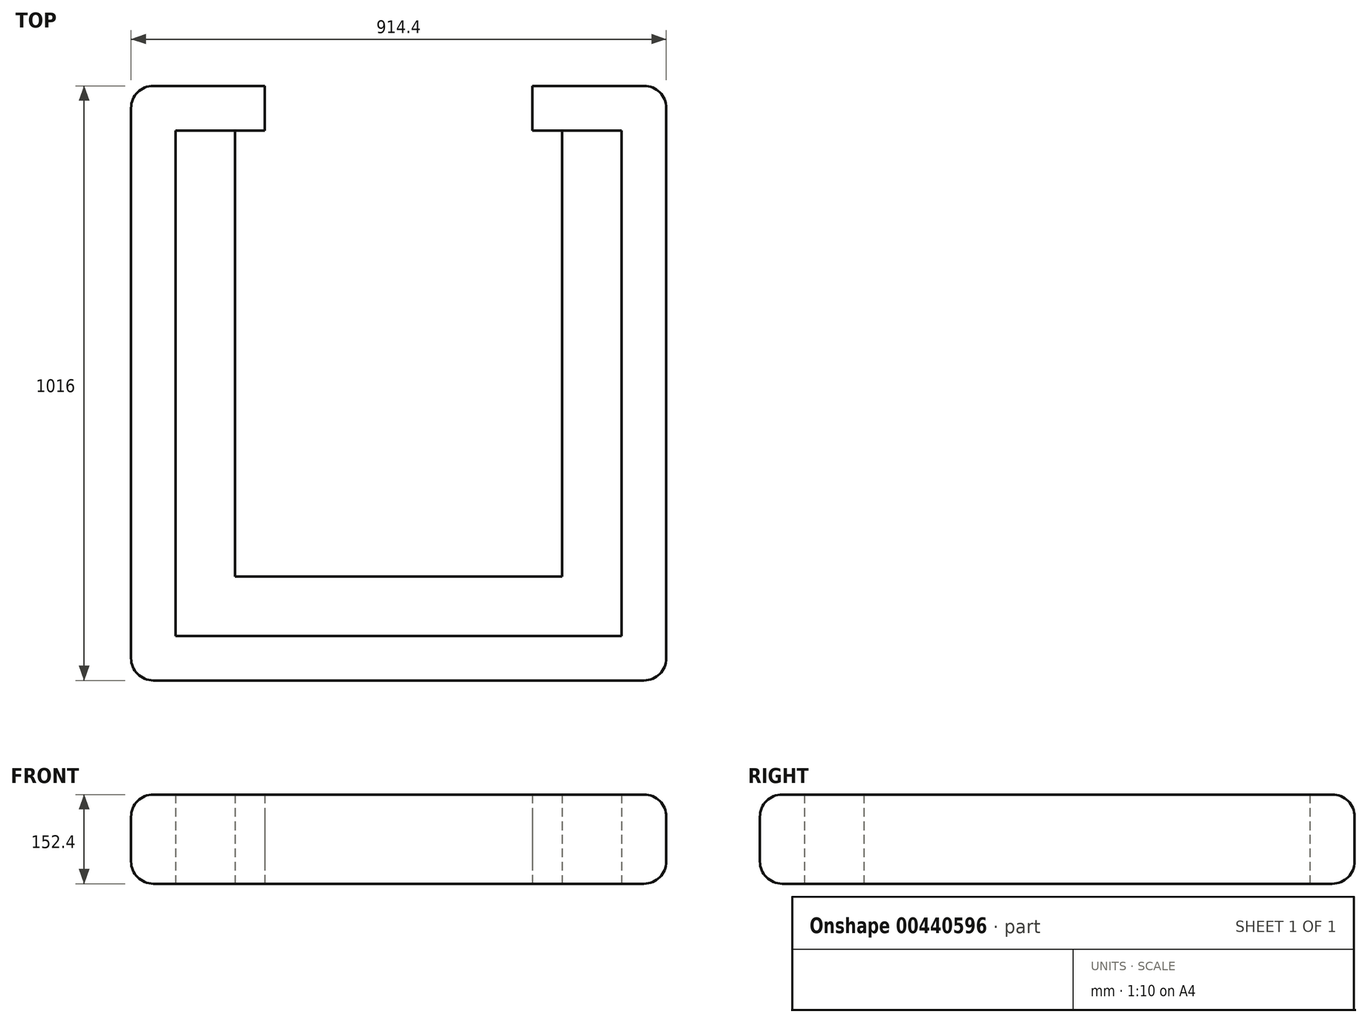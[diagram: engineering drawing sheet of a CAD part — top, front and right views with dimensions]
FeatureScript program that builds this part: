
annotation { "Feature Type Name" : "Feature", "Feature Type Description" : "" }
export const myFeature = defineFeature(function(context is Context, id is Id, definition is map)
    precondition{}
    {
        {
            var Q0;
            Q0=qCreatedBy(makeId("Top.planeOp"),FACE);
            var sketch = newSketch(context, id + "F0", { "sketchPlane" : qUnion([Q0])});
            skLineSegment(sketch, "E0.bottom", {"start": v(457.2, 508) * mm, "end": v(228.6, 508) * mm});
            skLineSegment(sketch, "E0.top", {"start": v(457.2, -508) * mm, "end": v(-457.2, -508) * mm});
            skLineSegment(sketch, "E0.left", {"start": v(457.2, 508) * mm, "end": v(457.2, -508) * mm});
            skLineSegment(sketch, "E0.right", {"start": v(-457.2, 508) * mm, "end": v(-457.2, -508) * mm});
            skPoint(sketch, "E0.middle", {"position": v(0, 0) * mm});
            skLineSegment(sketch, "E1.bottom", {"start": v(-381, 431.8) * mm, "end": v(-228.6, 431.8) * mm});
            skLineSegment(sketch, "E1.top", {"start": v(-381, -431.8) * mm, "end": v(381, -431.8) * mm});
            skLineSegment(sketch, "E1.left", {"start": v(-381, 431.8) * mm, "end": v(-381, -431.8) * mm});
            skLineSegment(sketch, "E1.right", {"start": v(381, 431.8) * mm, "end": v(381, -431.8) * mm});
            skLineSegment(sketch, "E2", {"start": v(-228.6, 431.8) * mm, "end": v(-228.6, 508) * mm});
            skLineSegment(sketch, "E3", {"start": v(228.6, 431.8) * mm, "end": v(228.6, 508) * mm});
            skLineSegment(sketch, "E4.trimOffspring", {"start": v(228.6, 431.8) * mm, "end": v(381, 431.8) * mm});
            skLineSegment(sketch, "E5.trimOffspring", {"start": v(-228.6, 508) * mm, "end": v(-457.2, 508) * mm});
            skSolve(sketch);
        }
        {
            var Q0;
            Q0=makeQuery(id+"F0.imprint","IMPRINT",FACE,{"disambiguationData":[TD([[makeQuery(id+"F0.imprint","IMPRINT",EDGE,{"derivedFrom":sQuery(id+"F0.wireOp",EDGE,"E0.bottom")}),1.0]])]});
            extrude(context, id + "F1", {"entities" : qUnion([Q0]), "depth" : 152.4 * mm});
        }
        {
            var Q0;
            Q0=makeQuery(id+"F1.opExtrude","CAP_EDGE",EDGE,{"disambiguationData":[OSD([sQuery(id+"F0.wireOp",EDGE,"E0.top")])],"isStart":false});
            var Q1;
            Q1=makeQuery(id+"F1.opExtrude","CAP_EDGE",EDGE,{"disambiguationData":[OSD([sQuery(id+"F0.wireOp",EDGE,"E0.right")])],"isStart":false});
            var Q2;
            Q2=makeQuery(id+"F1.opExtrude","SWEPT_EDGE",EDGE,{"disambiguationData":[OSD([sQuery(id+"F0.wireOp",EDGE,"E0.top"),sQuery(id+"F0.wireOp",EDGE,"E0.right")])]});
            var Q3;
            Q3=makeQuery(id+"F1.opExtrude","CAP_EDGE",EDGE,{"disambiguationData":[OSD([sQuery(id+"F0.wireOp",EDGE,"E0.top")])],"isStart":true});
            var Q4;
            Q4=makeQuery(id+"F1.opExtrude","SWEPT_EDGE",EDGE,{"disambiguationData":[OSD([sQuery(id+"F0.wireOp",EDGE,"E0.top"),sQuery(id+"F0.wireOp",EDGE,"E0.left")])]});
            var Q5;
            Q5=makeQuery(id+"F1.opExtrude","CAP_EDGE",EDGE,{"disambiguationData":[OSD([sQuery(id+"F0.wireOp",EDGE,"E0.left")])],"isStart":false});
            var Q6;
            Q6=makeQuery(id+"F1.opExtrude","CAP_EDGE",EDGE,{"disambiguationData":[OSD([sQuery(id+"F0.wireOp",EDGE,"E0.left")])],"isStart":true});
            var Q7;
            Q7=makeQuery(id+"F1.opExtrude","CAP_EDGE",EDGE,{"disambiguationData":[OSD([sQuery(id+"F0.wireOp",EDGE,"E0.bottom")])],"isStart":false});
            var Q8;
            Q8=makeQuery(id+"F1.opExtrude","CAP_EDGE",EDGE,{"disambiguationData":[OSD([sQuery(id+"F0.wireOp",EDGE,"E5.trimOffspring")])],"isStart":false});
            var Q9;
            Q9=makeQuery(id+"F1.opExtrude","CAP_EDGE",EDGE,{"disambiguationData":[OSD([sQuery(id+"F0.wireOp",EDGE,"E0.bottom")])],"isStart":true});
            var Q10;
            Q10=makeQuery(id+"F1.opExtrude","CAP_EDGE",EDGE,{"disambiguationData":[OSD([sQuery(id+"F0.wireOp",EDGE,"E5.trimOffspring")])],"isStart":true});
            var Q11;
            Q11=makeQuery(id+"F1.opExtrude","SWEPT_EDGE",EDGE,{"disambiguationData":[OSD([sQuery(id+"F0.wireOp",EDGE,"E0.bottom"),sQuery(id+"F0.wireOp",EDGE,"E0.left")])]});
            var Q12;
            Q12=makeQuery(id+"F1.opExtrude","SWEPT_EDGE",EDGE,{"disambiguationData":[OSD([sQuery(id+"F0.wireOp",EDGE,"E0.right"),sQuery(id+"F0.wireOp",EDGE,"E5.trimOffspring")])]});
            var Q13;
            Q13=makeQuery(id+"F1.opExtrude","CAP_EDGE",EDGE,{"disambiguationData":[OSD([sQuery(id+"F0.wireOp",EDGE,"E0.right")])],"isStart":true});
            fillet(context, id + "F2", {"entities" : qUnion([Q0, Q1, Q2, Q3, Q4, Q5, Q6, Q7, Q8, Q9, Q10, Q11, Q12, Q13]), "radius" : 38.1 * mm, "tangentPropagation" : true, "allowEdgeOverflow" : false});
        }
        {
            var Q0;
            Q0=qCreatedBy(makeId("Top.planeOp"),FACE);
            var sketch = newSketch(context, id + "F3", { "sketchPlane" : qUnion([Q0])});
            skLineSegment(sketch, "E6.0", {"start": v(-381, 431.8) * mm, "end": v(-381, -431.8) * mm});
            skLineSegment(sketch, "E7.0", {"start": v(-381, -431.8) * mm, "end": v(381, -431.8) * mm});
            skLineSegment(sketch, "E8.0", {"start": v(381, 431.8) * mm, "end": v(381, -431.8) * mm});
            skLineSegment(sketch, "E9", {"start": v(-381, 431.8) * mm, "end": v(-279.4, 431.8) * mm});
            skLineSegment(sketch, "E10", {"start": v(-279.4, 431.8) * mm, "end": v(-279.4, -330.2) * mm});
            skLineSegment(sketch, "E11", {"start": v(-279.4, -330.2) * mm, "end": v(279.4, -330.2) * mm});
            skLineSegment(sketch, "E12", {"start": v(279.4, -330.2) * mm, "end": v(279.4, 431.8) * mm});
            skLineSegment(sketch, "E13", {"start": v(279.4, 431.8) * mm, "end": v(381, 431.8) * mm});
            skSolve(sketch);
        }
        {
            var Q0;
            Q0=makeQuery(id+"F3.imprint","IMPRINT",FACE,{"disambiguationData":[TD([[makeQuery(id+"F3.imprint","IMPRINT",EDGE,{"derivedFrom":sQuery(id+"F3.wireOp",EDGE,"E6.0")}),1.0]])]});
            extrude(context, id + "F4", {"entities" : qUnion([Q0]), "depth" : 152.4 * mm});
        }
    });
